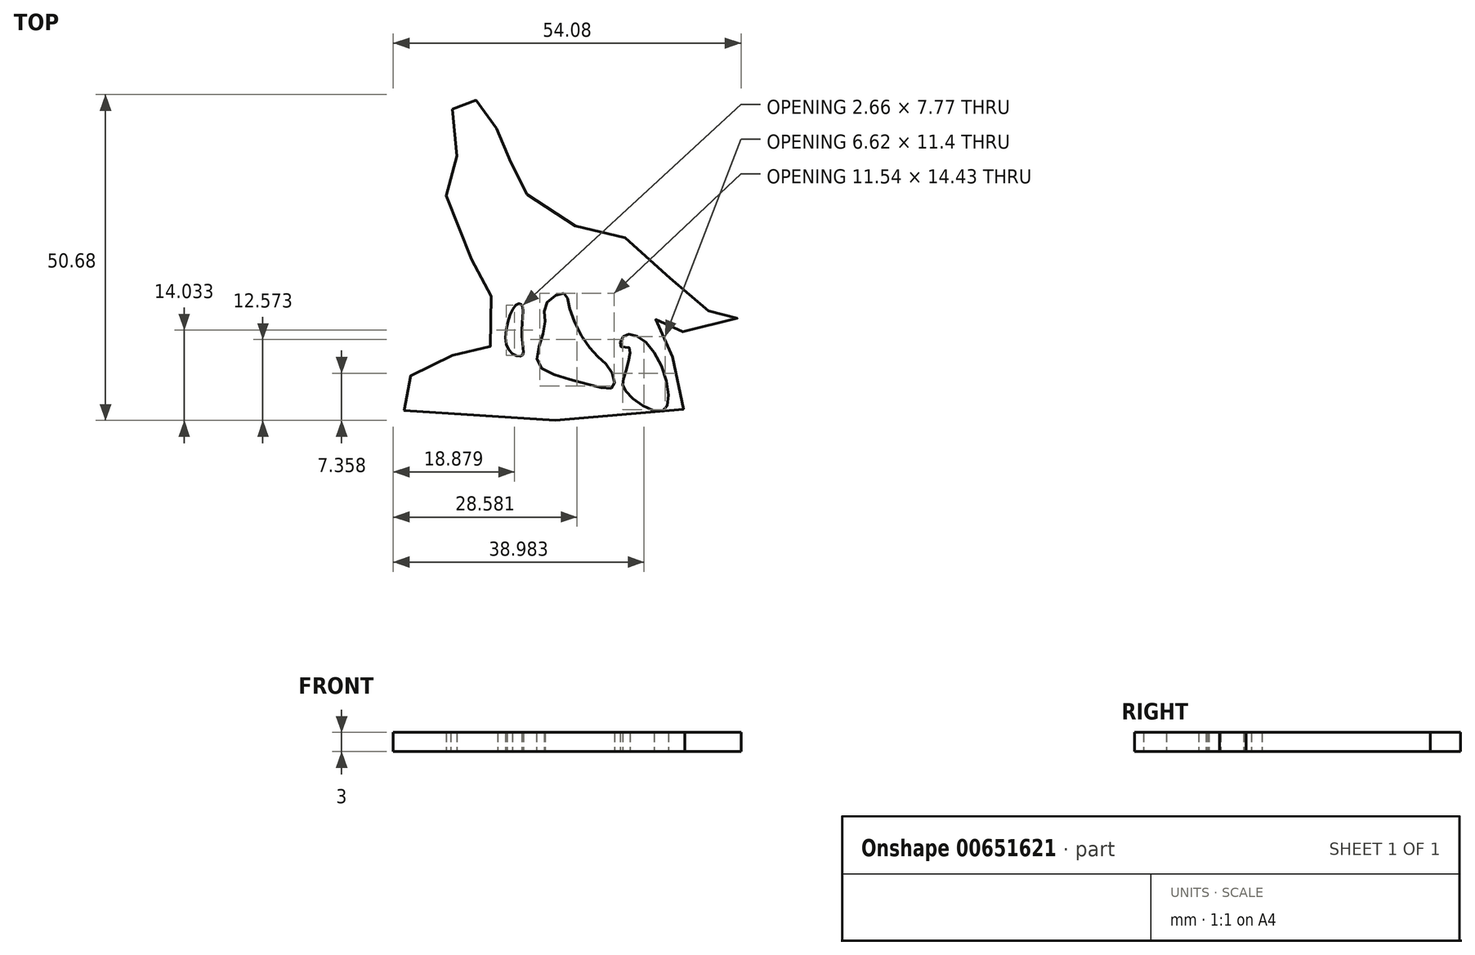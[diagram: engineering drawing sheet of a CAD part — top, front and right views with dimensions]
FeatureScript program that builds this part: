
annotation { "Feature Type Name" : "Feature", "Feature Type Description" : "" }
export const myFeature = defineFeature(function(context is Context, id is Id, definition is map)
    precondition{}
    {
        {
            var Q0;
            Q0=qCreatedBy(makeId("Top.planeOp"),FACE);
            var sketch = newSketch(context, id + "F0", { "sketchPlane" : qUnion([Q0])});
            skFitSpline(sketch, "E0", {"points": [v(9.07, 46.83) * mm, v(9.44, 41.78) * mm, v(9.63, 38.79) * mm, v(8.7, 37.86) * mm, v(9.25, 27.57) * mm, v(13.37, 21.78) * mm, v(14.67, 18.23) * mm, v(15.8, 16.92) * mm, v(14.86, 9.81) * mm, v(11.3, 10) * mm, v(8.13, 7.76) * mm, v(4.02, 6.45) * mm, v(0, 1.78) * mm, v(1.59, 0) * mm, v(44.77, 0) * mm, v(44.4, 2.71) * mm, v(42.9, 10.38) * mm, v(41.78, 11.87) * mm, v(40.47, 15.42) * mm, v(43.84, 12.8) * mm, v(50.94, 12.43) * mm, v(53.93, 15.6) * mm, v(49.82, 15.42) * mm, v(45.33, 17.67) * mm, v(41.03, 22.9) * mm, v(34.86, 27.2) * mm, v(30, 27.76) * mm, v(22.15, 33) * mm, v(19.9, 34.12) * mm, v(17.67, 38.23) * mm, v(18.41, 38.79) * mm, v(16.54, 41.78) * mm, v(15.6, 44.4) * mm, v(14.3, 44.59) * mm, v(12.24, 49.07) * mm, v(10.56, 47.95) * mm, v(9.07, 46.83) * mm]});
            skFitSpline(sketch, "E1", {"points": [v(26.45, 18.23) * mm, v(23.65, 16.54) * mm, v(23.46, 13) * mm, v(22.34, 7.38) * mm, v(29.07, 4.4) * mm, v(34.12, 3.65) * mm, v(33.56, 6.45) * mm, v(30.38, 9.81) * mm, v(27.2, 16.36) * mm, v(26.45, 18.23) * mm]});
            skFitSpline(sketch, "E2", {"points": [v(35.61, 11.5) * mm, v(35.42, 9.81) * mm, v(36.55, 9.81) * mm, v(35.99, 5.89) * mm, v(35.99, 3.08) * mm, v(41.97, 0) * mm, v(39.91, 9.81) * mm, v(35.61, 11.5) * mm]});
            skFitSpline(sketch, "E3", {"points": [v(18.97, 16.36) * mm, v(19.9, 16.36) * mm, v(19.9, 11.5) * mm, v(19.9, 8.5) * mm, v(17.67, 9.81) * mm, v(18.97, 16.36) * mm]});
            skSolve(sketch);
        }
        {
            var Q0;
            Q0=makeQuery(id+"F0.imprint","IMPRINT",FACE,{"disambiguationData":[TD([[makeQuery(id+"F0.imprint","IMPRINT",EDGE,{"derivedFrom":sQuery(id+"F0.wireOp",EDGE,"E0")}),1.0]])]});
            extrude(context, id + "F1", {"entities" : qUnion([Q0]), "depth" : 3 * mm, "offsetDistance" : 25.4 * mm});
        }
    });
